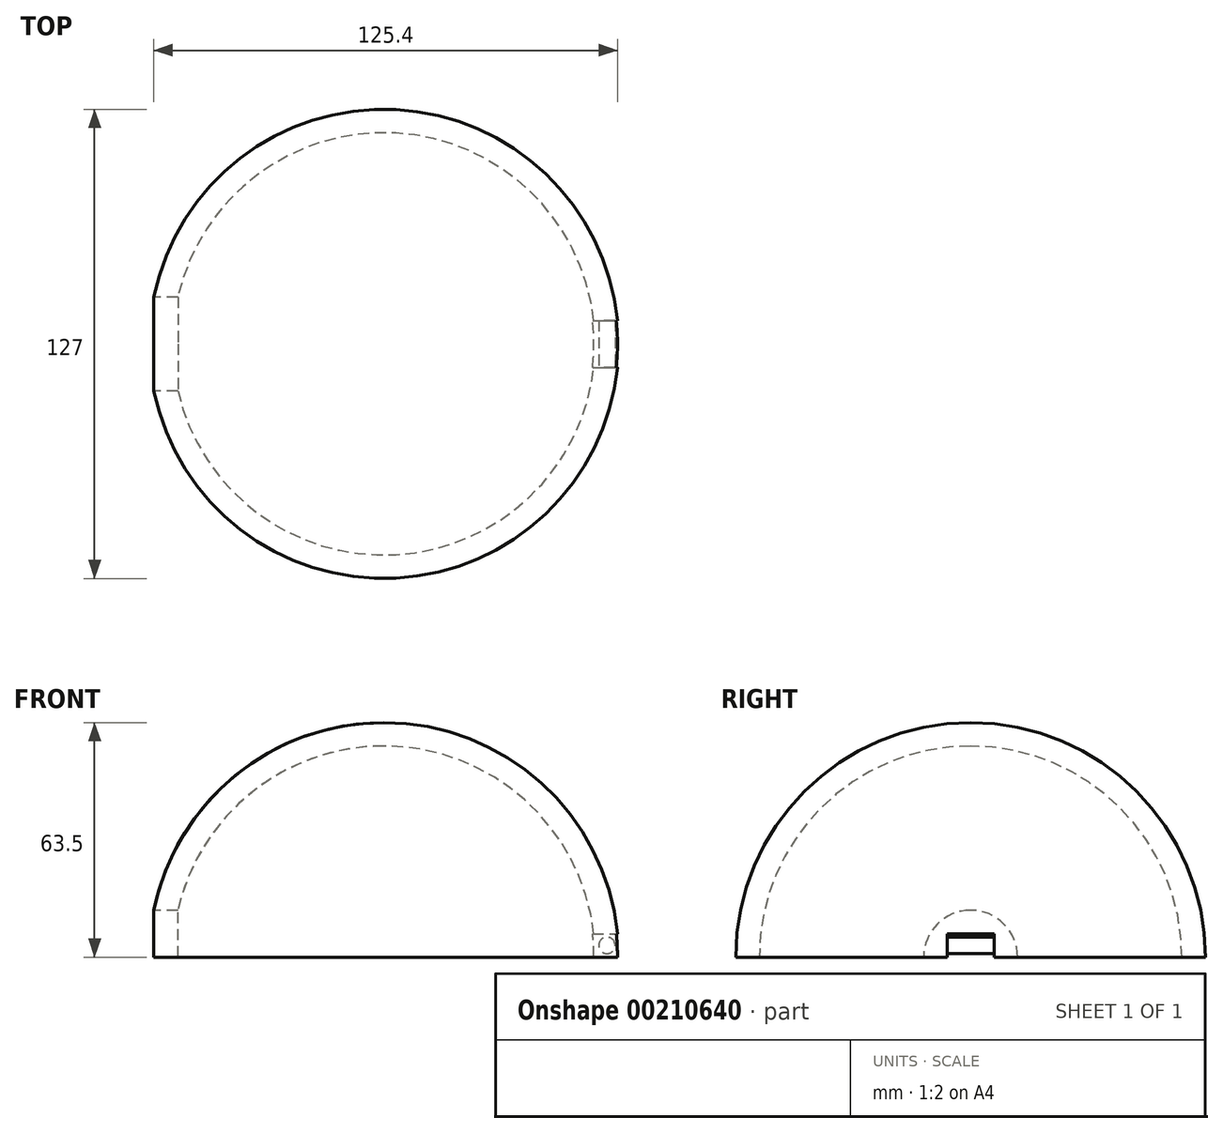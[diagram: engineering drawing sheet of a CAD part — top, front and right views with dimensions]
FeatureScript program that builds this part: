
annotation { "Feature Type Name" : "Feature", "Feature Type Description" : "" }
export const myFeature = defineFeature(function(context is Context, id is Id, definition is map)
    precondition{}
    {
        {
            var Q0;
            Q0=qCreatedBy(makeId("Front.planeOp"),FACE);
            var sketch = newSketch(context, id + "F0", { "sketchPlane" : qUnion([Q0])});
            skArc(sketch, "E0", {"start": v(0, 63.5) * mm, "mid": v(-44.9, 44.9) * mm, "end": v(-63.5, 0) * mm});
            skLineSegment(sketch, "E1", {"start": v(-63.5, 0) * mm, "end": v(-57.15, 0) * mm});
            skLineSegment(sketch, "E2", {"start": v(0, 57.15) * mm, "end": v(0, 63.5) * mm});
            skArc(sketch, "E3.0", {"start": v(0, 57.15) * mm, "mid": v(-40.41, 40.41) * mm, "end": v(-57.15, 0) * mm});
            skSolve(sketch);
        }
        {
            var Q0;
            Q0=makeQuery(id+"F0.imprint","IMPRINT",FACE,{"disambiguationData":[TD([[makeQuery(id+"F0.imprint","IMPRINT",EDGE,{"derivedFrom":sQuery(id+"F0.wireOp",EDGE,"E0")}),1.0]])]});
            var Q1;
            Q1=sQuery(id+"F0.wireOp",EDGE,"E2");
            revolve(context, id + "F1", {"entities" : qUnion([Q0]), "axis" : qUnion([Q1]), "revolveType" : RevolveType.FULL});
        }
        {
            var Q0;
            Q0=qCreatedBy(makeId("Front.planeOp"),FACE);
            var sketch = newSketch(context, id + "F2", { "sketchPlane" : qUnion([Q0])});
            skArc(sketch, "E4", {"start": v(63.5, 0) * mm, "mid": v(0, 63.5) * mm, "end": v(-63.5, 0) * mm, "construction": true});
            skArc(sketch, "E5", {"start": v(63.5, 0) * mm, "mid": v(0, 63.5) * mm, "end": v(-63.5, 0) * mm});
            skArc(sketch, "E6", {"start": v(57.15, 0) * mm, "mid": v(0, 57.15) * mm, "end": v(-57.15, 0) * mm, "construction": true});
            skCircle(sketch, "E7", {"center": v(60.33, 3.17) * mm, "radius": 2.22 * mm});
            skLineSegment(sketch, "E8.bottom", {"start": v(55.22, 6.35) * mm, "end": v(66.22, 6.35) * mm});
            skLineSegment(sketch, "E8.top", {"start": v(55.22, -2.16) * mm, "end": v(66.22, -2.16) * mm});
            skLineSegment(sketch, "E8.left", {"start": v(55.22, 6.35) * mm, "end": v(55.22, -2.16) * mm});
            skLineSegment(sketch, "E8.right", {"start": v(66.22, 6.35) * mm, "end": v(66.22, -2.16) * mm});
            skSolve(sketch);
        }
        {
            var Q0;
            Q0=makeQuery(id+"F2.imprint","IMPRINT",FACE,{"disambiguationData":[TD([[makeQuery(id+"F2.imprint","IMPRINT",EDGE,{"derivedFrom":sQuery(id+"F2.wireOp",EDGE,"E7")}),-1.0]])]});
            extrude(context, id + "F3", {"entities" : qUnion([Q0]), "operationType" : NewBodyOperationType.REMOVE, "endBound" : BoundingType.SYMMETRIC, "oppositeDirection" : true, "depth" : 12.7 * mm});
        }
        {
            var Q0;
            Q0=qCreatedBy(makeId("Right.planeOp"),FACE);
            cPlane(context, id + "F4", {"entities" : qUnion([Q0]), "cplaneType" : CPlaneType.OFFSET, "offset" : 63.5 * mm, "oppositeDirection" : true, "width" : 152.4 * mm, "height" : 152.4 * mm});
        }
        {
            var Q0;
            Q0=qCreatedBy(id+"F4.planeOp",FACE);
            var sketch = newSketch(context, id + "F5", { "sketchPlane" : qUnion([Q0])});
            skCircle(sketch, "E9", {"center": v(0, 0) * mm, "radius": 12.7 * mm});
            skSolve(sketch);
        }
        {
            var Q0;
            Q0=makeQuery(id+"F5.imprint","IMPRINT",FACE,{"disambiguationData":[TD([[makeQuery(id+"F5.imprint","IMPRINT",EDGE,{"derivedFrom":sQuery(id+"F5.wireOp",EDGE,"E9")}),1.0]])]});
            extrude(context, id + "F6", {"entities" : qUnion([Q0]), "operationType" : NewBodyOperationType.REMOVE, "depth" : 25.4 * mm});
        }
    });
